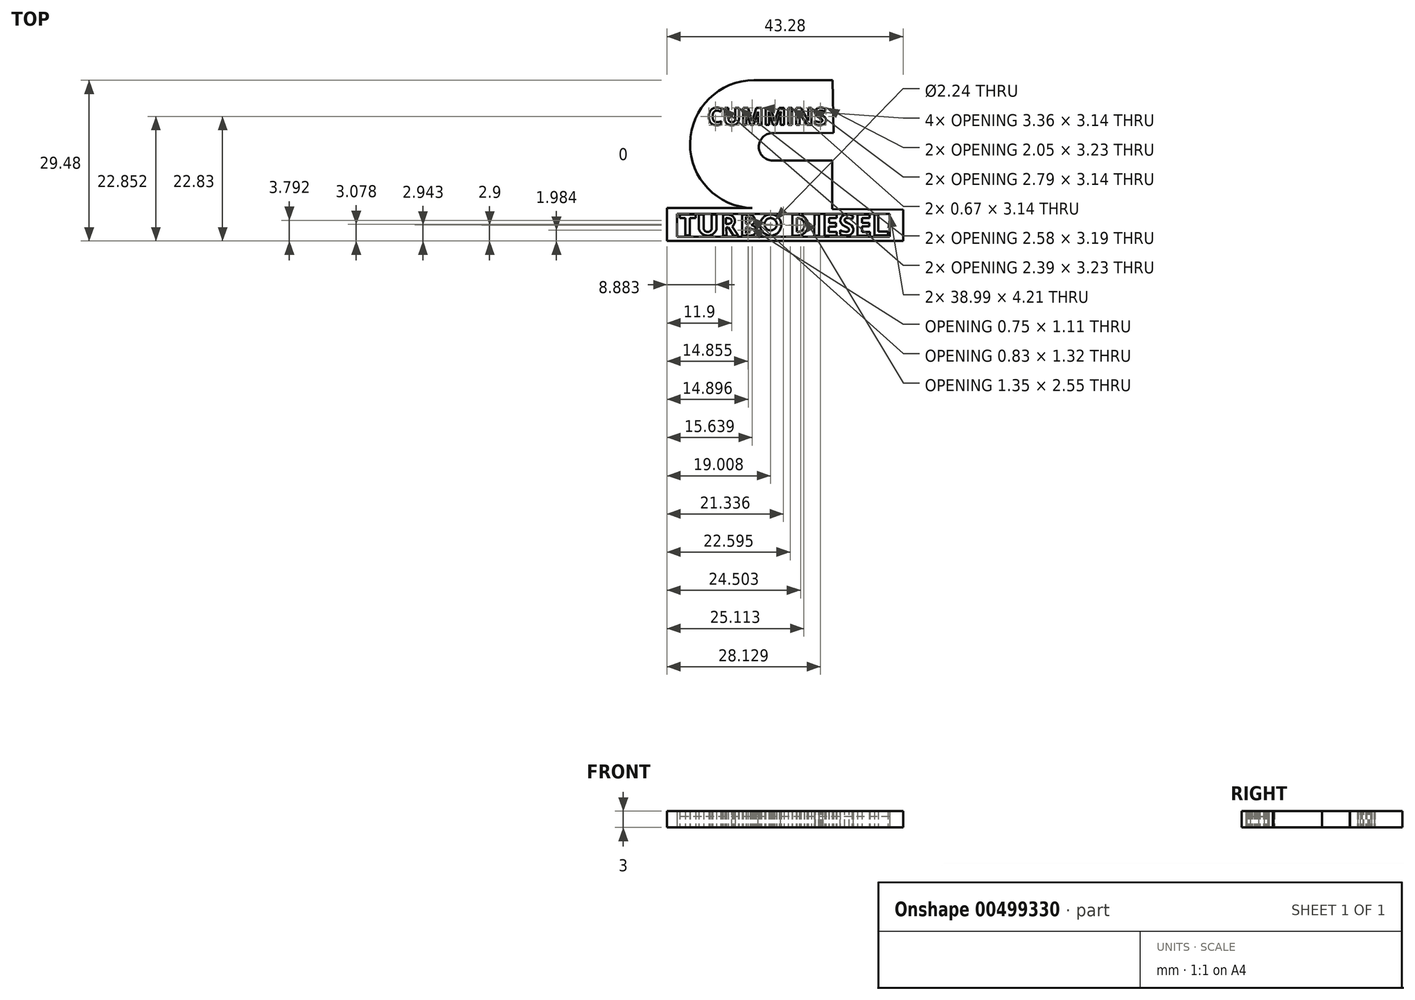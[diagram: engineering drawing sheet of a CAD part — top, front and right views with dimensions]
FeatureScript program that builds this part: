
annotation { "Feature Type Name" : "Feature", "Feature Type Description" : "" }
export const myFeature = defineFeature(function(context is Context, id is Id, definition is map)
    precondition{}
    {
        {
            var Q0;
            Q0=qCreatedBy(makeId("Top.planeOp"),FACE);
            var sketch = newSketch(context, id + "F0", { "sketchPlane" : qUnion([Q0])});
            skLineSegment(sketch, "E0", {"start": v(-58.17, -40.48) * mm, "end": v(-14.89, -40.48) * mm});
            skLineSegment(sketch, "E1", {"start": v(-14.89, -40.48) * mm, "end": v(-14.89, -34.72) * mm});
            skLineSegment(sketch, "E2", {"start": v(-14.89, -34.72) * mm, "end": v(-27.85, -34.6) * mm});
            skLineSegment(sketch, "E3", {"start": v(-27.85, -34.6) * mm, "end": v(-27.85, -25.72) * mm});
            skFitSpline(sketch, "E4", {"points": [v(-27.65, -20.6) * mm, v(-38.88, -20.67) * mm], "startDerivative": vector(-11.23, -0.07) * mm, "endDerivative": vector(-11.23, -0.07) * mm});
            skFitSpline(sketch, "E5", {"points": [v(-27.82, -11) * mm, v(-27.65, -20.6) * mm], "startDerivative": vector(0.17, -9.61) * mm, "endDerivative": vector(0.17, -9.61) * mm});
            skLineSegment(sketch, "E6", {"start": v(-42.53, -34.43) * mm, "end": v(-27.85, -34.6) * mm});
            skLineSegment(sketch, "E7", {"start": v(-27.85, -25.72) * mm, "end": v(-38.8, -25.72) * mm});
            skLineSegment(sketch, "E8", {"start": v(-55.83, -35.61) * mm, "end": v(-55.83, -36.28) * mm});
            skLineSegment(sketch, "E9", {"start": v(-55.83, -36.28) * mm, "end": v(-54.78, -36.28) * mm});
            skLineSegment(sketch, "E10", {"start": v(-54.78, -36.28) * mm, "end": v(-54.78, -39.44) * mm});
            skLineSegment(sketch, "E11", {"start": v(-53.95, -39.44) * mm, "end": v(-53.95, -36.28) * mm});
            skLineSegment(sketch, "E12", {"start": v(-53.95, -36.28) * mm, "end": v(-52.88, -36.28) * mm});
            skLineSegment(sketch, "E13", {"start": v(-52.88, -36.28) * mm, "end": v(-52.88, -35.61) * mm});
            skLineSegment(sketch, "E14", {"start": v(-52.88, -35.61) * mm, "end": v(-55.83, -35.61) * mm});
            skPoint(sketch, "E15", {"position": v(-50.74, -19.2) * mm});
            skText(sketch, "E16", { "text": "CUMMINS", "fontName": "OpenSans-Bold.ttf"});
            skPoint(sketch, "E17", {"position": v(-47.5, -22.36) * mm});
            skLineSegment(sketch, "E18", {"start": v(-47.87, -39.47) * mm, "end": v(-47.22, -39.48) * mm});
            skLineSegment(sketch, "E19", {"start": v(-47.22, -39.48) * mm, "end": v(-47.34, -38) * mm});
            skLineSegment(sketch, "E20", {"start": v(-47.34, -38) * mm, "end": v(-46.9, -38) * mm});
            skLineSegment(sketch, "E21", {"start": v(-46.9, -38) * mm, "end": v(-46, -39.47) * mm});
            skLineSegment(sketch, "E22", {"start": v(-46, -39.47) * mm, "end": v(-45.07, -39.47) * mm});
            skLineSegment(sketch, "E23", {"start": v(-45.07, -39.47) * mm, "end": v(-46.2, -37.8) * mm});
            skLineSegment(sketch, "E24", {"start": v(-52.34, -35.65) * mm, "end": v(-51.45, -35.65) * mm});
            skLineSegment(sketch, "E25", {"start": v(-49.95, -35.6) * mm, "end": v(-49.07, -35.6) * mm});
            skLineSegment(sketch, "E26", {"start": v(-49.95, -35.6) * mm, "end": v(-49.95, -38.21) * mm});
            skPoint(sketch, "E27.7.internal.snap0", {"position": v(-46.45, -38.74) * mm});
            skLineSegment(sketch, "E28", {"start": v(-47.35, -36.28) * mm, "end": v(-47.35, -37.32) * mm});
            skLineSegment(sketch, "E29", {"start": v(-47.35, -36.28) * mm, "end": v(-46.92, -36.28) * mm});
            skFitSpline(sketch, "E30", {"points": [v(-47.35, -37.32) * mm, v(-47.07, -37.32) * mm, v(-46.97, -37.32) * mm, v(-46.66, -37.29) * mm, v(-46.45, -37.16) * mm, v(-46.33, -36.95) * mm, v(-46.32, -36.72) * mm, v(-46.37, -36.55) * mm, v(-46.47, -36.43) * mm, v(-46.6, -36.35) * mm, v(-46.77, -36.3) * mm, v(-46.92, -36.28) * mm], "startDerivative": vector(3.02, 0) * mm, "endDerivative": vector(-1.87, 0.24) * mm});
            skPoint(sketch, "E31.first.point", {"position": v(-38.93, -39.47) * mm});
            skPoint(sketch, "E31.second.point", {"position": v(-38.68, -35.65) * mm});
            skPoint(sketch, "E31.third.point", {"position": v(-41.08, -37.34) * mm});
            skLineSegment(sketch, "E32", {"start": v(-34.34, -36.26) * mm, "end": v(-34.34, -38.8) * mm});
            skLineSegment(sketch, "E33", {"start": v(-31.14, -35.65) * mm, "end": v(-30.31, -35.65) * mm});
            skLineSegment(sketch, "E34", {"start": v(-30.31, -35.65) * mm, "end": v(-30.31, -39.47) * mm});
            skLineSegment(sketch, "E35", {"start": v(-30.31, -39.47) * mm, "end": v(-31.16, -39.47) * mm});
            skLineSegment(sketch, "E36", {"start": v(-31.16, -39.47) * mm, "end": v(-31.14, -35.65) * mm});
            skLineSegment(sketch, "E37", {"start": v(-28.47, -36.27) * mm, "end": v(-27.02, -36.27) * mm});
            skLineSegment(sketch, "E38", {"start": v(-27.02, -36.27) * mm, "end": v(-27.02, -35.65) * mm});
            skLineSegment(sketch, "E39", {"start": v(-27.02, -35.65) * mm, "end": v(-29.3, -35.65) * mm});
            skLineSegment(sketch, "E40", {"start": v(-29.3, -35.65) * mm, "end": v(-29.3, -39.47) * mm});
            skLineSegment(sketch, "E41", {"start": v(-29.3, -39.47) * mm, "end": v(-27.07, -39.47) * mm});
            skLineSegment(sketch, "E42", {"start": v(-27.07, -39.47) * mm, "end": v(-27.07, -38.8) * mm});
            skLineSegment(sketch, "E43", {"start": v(-27.07, -38.8) * mm, "end": v(-28.5, -38.8) * mm});
            skLineSegment(sketch, "E44", {"start": v(-28.5, -38.8) * mm, "end": v(-28.5, -37.84) * mm});
            skLineSegment(sketch, "E45", {"start": v(-28.5, -37.84) * mm, "end": v(-27.18, -37.84) * mm});
            skLineSegment(sketch, "E46", {"start": v(-27.18, -37.84) * mm, "end": v(-27.18, -37.12) * mm});
            skLineSegment(sketch, "E47", {"start": v(-27.18, -37.12) * mm, "end": v(-28.52, -37.12) * mm});
            skLineSegment(sketch, "E48", {"start": v(-28.47, -36.27) * mm, "end": v(-28.47, -37.12) * mm});
            skLineSegment(sketch, "E49", {"start": v(-23.26, -39.48) * mm, "end": v(-20.98, -39.48) * mm});
            skLineSegment(sketch, "E50", {"start": v(-20.98, -38.77) * mm, "end": v(-22.42, -38.77) * mm});
            skLineSegment(sketch, "E51", {"start": v(-22.42, -38.77) * mm, "end": v(-22.42, -37.81) * mm});
            skLineSegment(sketch, "E52", {"start": v(-22.42, -37.81) * mm, "end": v(-21.1, -37.81) * mm});
            skLineSegment(sketch, "E53", {"start": v(-21.1, -37.81) * mm, "end": v(-21.1, -37.13) * mm});
            skLineSegment(sketch, "E54", {"start": v(-21.1, -37.13) * mm, "end": v(-22.44, -37.13) * mm});
            skLineSegment(sketch, "E55", {"start": v(-22.44, -37.13) * mm, "end": v(-22.44, -36.27) * mm});
            skLineSegment(sketch, "E56", {"start": v(-22.44, -36.27) * mm, "end": v(-21, -36.27) * mm});
            skLineSegment(sketch, "E57", {"start": v(-21, -36.27) * mm, "end": v(-21, -35.61) * mm});
            skLineSegment(sketch, "E58", {"start": v(-23.24, -35.61) * mm, "end": v(-23.24, -36.44) * mm});
            skLineSegment(sketch, "E59", {"start": v(-23.24, -36.44) * mm, "end": v(-23.26, -39.48) * mm});
            skLineSegment(sketch, "E60", {"start": v(-20.14, -35.65) * mm, "end": v(-19.4, -35.65) * mm});
            skLineSegment(sketch, "E61", {"start": v(-42.53, -34.43) * mm, "end": v(-58.17, -34.43) * mm});
            skLineSegment(sketch, "E62", {"start": v(-58.17, -34.43) * mm, "end": v(-58.17, -40.48) * mm});
            skLineSegment(sketch, "E63", {"start": v(-54.78, -39.44) * mm, "end": v(-54.78, -39.47) * mm});
            skLineSegment(sketch, "E64", {"start": v(-54.78, -39.47) * mm, "end": v(-53.95, -39.47) * mm});
            skLineSegment(sketch, "E65", {"start": v(-53.95, -39.44) * mm, "end": v(-53.95, -39.47) * mm});
            skLineSegment(sketch, "E66", {"start": v(-52.34, -35.65) * mm, "end": v(-52.34, -38.14) * mm});
            skLineSegment(sketch, "E67", {"start": v(-51.45, -35.65) * mm, "end": v(-51.45, -38.14) * mm});
            skLineSegment(sketch, "E68", {"start": v(-49.07, -35.6) * mm, "end": v(-49.07, -38.21) * mm});
            skArc(sketch, "E69", {"start": v(-51.45, -38.14) * mm, "mid": v(-50.73, -38.81) * mm, "end": v(-49.95, -38.21) * mm});
            skArc(sketch, "E70", {"start": v(-52.34, -38.14) * mm, "mid": v(-50.73, -39.5) * mm, "end": v(-49.07, -38.21) * mm});
            skLineSegment(sketch, "E71", {"start": v(-44.38, -35.65) * mm, "end": v(-44.38, -39.47) * mm});
            skLineSegment(sketch, "E72", {"start": v(-44.38, -35.65) * mm, "end": v(-43.04, -35.65) * mm});
            skArc(sketch, "E73", {"start": v(-42.74, -37.56) * mm, "mid": v(-42.07, -36.48) * mm, "end": v(-43.04, -35.65) * mm});
            skPoint(sketch, "E73.startSnap0", {"position": v(-44.38, -37.56) * mm});
            skLineSegment(sketch, "E74", {"start": v(-44.38, -39.47) * mm, "end": v(-42.76, -39.46) * mm});
            skArc(sketch, "E75", {"start": v(-42.76, -39.46) * mm, "mid": v(-41.8, -38.52) * mm, "end": v(-42.74, -37.56) * mm});
            skCircle(sketch, "E76", {"center": v(-39.16, -37.4) * mm, "radius": 1.12 * mm});
            skLineSegment(sketch, "E77", {"start": v(-35.15, -35.65) * mm, "end": v(-35.15, -39.47) * mm});
            skLineSegment(sketch, "E78", {"start": v(-35.15, -35.65) * mm, "end": v(-34.21, -35.65) * mm});
            skLineSegment(sketch, "E79", {"start": v(-35.15, -39.47) * mm, "end": v(-34.21, -39.47) * mm});
            skArc(sketch, "E80", {"start": v(-32.99, -37.53) * mm, "mid": v(-33.38, -36.59) * mm, "end": v(-34.34, -36.26) * mm});
            skArc(sketch, "E81", {"start": v(-34.34, -38.8) * mm, "mid": v(-33.36, -38.5) * mm, "end": v(-32.99, -37.53) * mm});
            skLineSegment(sketch, "E82", {"start": v(-27.82, -11) * mm, "end": v(-42.2, -11) * mm});
            skArc(sketch, "E83", {"start": v(-42.2, -11) * mm, "mid": v(-53.93, -22.55) * mm, "end": v(-42.53, -34.43) * mm});
            skArc(sketch, "E84", {"start": v(-38.88, -20.67) * mm, "mid": v(-41.32, -23.24) * mm, "end": v(-38.8, -25.72) * mm});
            skLineSegment(sketch, "E85", {"start": v(-47.87, -39.47) * mm, "end": v(-47.87, -35.65) * mm});
            skLineSegment(sketch, "E86", {"start": v(-46.9, -35.65) * mm, "end": v(-47.87, -35.65) * mm});
            skArc(sketch, "E87", {"start": v(-46.2, -37.8) * mm, "mid": v(-45.77, -36.47) * mm, "end": v(-46.9, -35.65) * mm});
            skArc(sketch, "E88", {"start": v(-38.93, -39.47) * mm, "mid": v(-37.22, -37.66) * mm, "end": v(-38.68, -35.65) * mm});
            skArc(sketch, "E89", {"start": v(-38.68, -35.65) * mm, "mid": v(-41.08, -37.41) * mm, "end": v(-38.93, -39.47) * mm});
            skArc(sketch, "E90", {"start": v(-34.21, -39.47) * mm, "mid": v(-32.3, -37.56) * mm, "end": v(-34.21, -35.65) * mm});
            skArc(sketch, "E91", {"start": v(-52.34, -38.14) * mm, "mid": v(-50.73, -39.49) * mm, "end": v(-49.07, -38.21) * mm});
            skLineSegment(sketch, "E92", {"start": v(-47.87, -35.65) * mm, "end": v(-47.87, -39.47) * mm});
            skLineSegment(sketch, "E93", {"start": v(-47.87, -35.65) * mm, "end": v(-46.9, -35.65) * mm});
            skLineSegment(sketch, "E94", {"start": v(-46.2, -37.8) * mm, "end": v(-45.07, -39.47) * mm});
            skLineSegment(sketch, "E95", {"start": v(-46, -39.47) * mm, "end": v(-46.9, -38) * mm});
            skLineSegment(sketch, "E96", {"start": v(-47.34, -38) * mm, "end": v(-47.22, -39.48) * mm});
            skCircle(sketch, "E97", {"center": v(-39.16, -37.4) * mm, "radius": 1.11 * mm});
            skLineSegment(sketch, "E98", {"start": v(-43.7, -36.03) * mm, "end": v(-43.7, -37.35) * mm});
            skArc(sketch, "E99", {"start": v(-43.7, -37.35) * mm, "mid": v(-42.86, -36.69) * mm, "end": v(-43.7, -36.03) * mm});
            skLineSegment(sketch, "E100", {"start": v(-43.7, -37.97) * mm, "end": v(-43.68, -39.02) * mm});
            skArc(sketch, "E101", {"start": v(-43.68, -39.02) * mm, "mid": v(-42.94, -38.5) * mm, "end": v(-43.7, -37.97) * mm});
            skLineSegment(sketch, "E102", {"start": v(-24.01, -35.87) * mm, "end": v(-24.27, -36.49) * mm});
            skFitSpline(sketch, "E103", {"points": [v(-24.27, -36.49) * mm, v(-24.4, -36.44) * mm, v(-24.56, -36.38) * mm, v(-24.76, -36.32) * mm, v(-24.94, -36.29) * mm, v(-25.02, -36.28) * mm, v(-25.23, -36.27) * mm, v(-25.37, -36.3) * mm, v(-25.5, -36.36) * mm, v(-25.6, -36.54) * mm, v(-25.6, -36.74) * mm, v(-25.54, -36.87) * mm, v(-25.4, -37) * mm, v(-24.71, -37.35) * mm, v(-24.27, -37.65) * mm, v(-24.04, -38.02) * mm, v(-23.99, -38.37) * mm, v(-24.06, -38.8) * mm, v(-24.27, -39.1) * mm, v(-24.56, -39.3) * mm, v(-24.9, -39.41) * mm, v(-25.14, -39.46) * mm, v(-25.3, -39.46) * mm, v(-25.47, -39.46) * mm, v(-25.78, -39.44) * mm, v(-26.08, -39.38) * mm, v(-26.44, -39.24) * mm], "startDerivative": vector(-4.34, 1.57) * mm, "endDerivative": vector(-7.91, 3.38) * mm});
            skLineSegment(sketch, "E104", {"start": v(-26.44, -38.5) * mm, "end": v(-26.44, -39.24) * mm});
            skFitSpline(sketch, "E105", {"points": [v(-26.44, -38.5) * mm, v(-26, -38.68) * mm, v(-25.71, -38.76) * mm, v(-25.38, -38.8) * mm, v(-25.17, -38.8) * mm, v(-24.99, -38.75) * mm, v(-24.87, -38.67) * mm, v(-24.8, -38.56) * mm, v(-24.77, -38.38) * mm, v(-24.83, -38.22) * mm, v(-24.93, -38.12) * mm, v(-25.1, -38) * mm, v(-25.23, -37.93) * mm, v(-25.83, -37.63) * mm, v(-26.22, -37.27) * mm, v(-26.38, -36.85) * mm, v(-26.38, -36.47) * mm, v(-26.23, -36.1) * mm, v(-26, -35.85) * mm, v(-25.74, -35.7) * mm, v(-25.37, -35.62) * mm, v(-25.21, -35.61) * mm, v(-25.13, -35.61) * mm, v(-25, -35.61) * mm, v(-24.96, -35.61) * mm, v(-24.68, -35.65) * mm, v(-24.42, -35.72) * mm, v(-24.01, -35.87) * mm], "startDerivative": vector(9.09, -3.88) * mm, "endDerivative": vector(9.18, -3.55) * mm});
            skLineSegment(sketch, "E106", {"start": v(-23.24, -35.61) * mm, "end": v(-21, -35.61) * mm});
            skLineSegment(sketch, "E107", {"start": v(-20.14, -35.65) * mm, "end": v(-20.14, -39.42) * mm});
            skLineSegment(sketch, "E108", {"start": v(-20.14, -39.42) * mm, "end": v(-17.67, -39.42) * mm});
            skLineSegment(sketch, "E109", {"start": v(-17.67, -39.42) * mm, "end": v(-17.67, -38.72) * mm});
            skLineSegment(sketch, "E110", {"start": v(-17.67, -38.72) * mm, "end": v(-19.42, -38.72) * mm});
            skLineSegment(sketch, "E111", {"start": v(-19.42, -38.72) * mm, "end": v(-19.4, -35.65) * mm});
            skLineSegment(sketch, "E112", {"start": v(-19.4, -35.65) * mm, "end": v(-20.14, -35.65) * mm});
            skLineSegment(sketch, "E113", {"start": v(-56.33, -35.47) * mm, "end": v(-56.33, -39.69) * mm});
            skLineSegment(sketch, "E114", {"start": v(-56.33, -39.69) * mm, "end": v(-17.34, -39.69) * mm});
            skLineSegment(sketch, "E115", {"start": v(-17.34, -39.69) * mm, "end": v(-17.34, -35.48) * mm});
            skLineSegment(sketch, "E116", {"start": v(-17.34, -35.48) * mm, "end": v(-56.33, -35.47) * mm});
            skLineSegment(sketch, "E117", {"start": v(-20.98, -38.77) * mm, "end": v(-20.98, -39.48) * mm});
            skLineSegment(sketch, "E118", {"start": v(-52.88, -35.61) * mm, "end": v(-52.88, -36.28) * mm});
            skLineSegment(sketch, "E119", {"start": v(-54.78, -39.44) * mm, "end": v(-53.95, -39.44) * mm});
            const initialGuessF0  = {"E16": [-0.05074, -0.0192, 1, 0, 0.00317]};
            skSetInitialGuess(sketch, initialGuessF0);
            skSolve(sketch);
        }
        {
            var Q0;
            {var subQ25=sQuery(id+"F0.wireOp",EDGE,"30c9a4f5-6872-4423-ba19-b8290065d747.sketch_text.stroke-0");Q0=makeQuery(id+"F0.imprint","IMPRINT",FACE,{"disambiguationData":[TD([[makeQuery(id+"F0.imprint","IMPRINT",EDGE,{"derivedFrom":subQ25}),-1.0]])]});}
            var Q1;
            Q1=makeQuery(id+"F0.imprint","IMPRINT",FACE,{"disambiguationData":[TD([[makeQuery(id+"F0.imprint","IMPRINT",EDGE,{"derivedFrom":sQuery(id+"F0.wireOp",EDGE,"E37")}),1.0]])]});
            var Q2;
            Q2=makeQuery(id+"F0.imprint","IMPRINT",FACE,{"disambiguationData":[TD([[makeQuery(id+"F0.imprint","IMPRINT",EDGE,{"derivedFrom":sQuery(id+"F0.wireOp",EDGE,"E33")}),-1.0]])]});
            var Q3;
            Q3=makeQuery(id+"F0.imprint","IMPRINT",FACE,{"disambiguationData":[TD([[makeQuery(id+"F0.imprint","IMPRINT",EDGE,{"derivedFrom":sQuery(id+"F0.wireOp",EDGE,"E32")}),-1.0]])]});
            var Q4;
            Q4=makeQuery(id+"F0.imprint","IMPRINT",FACE,{"disambiguationData":[TD([[makeQuery(id+"F0.imprint","IMPRINT",EDGE,{"derivedFrom":sQuery(id+"F0.wireOp",EDGE,"E76")}),-1.0]])]});
            var Q5;
            Q5=makeQuery(id+"F0.imprint","IMPRINT",FACE,{"disambiguationData":[TD([[makeQuery(id+"F0.imprint","IMPRINT",EDGE,{"derivedFrom":sQuery(id+"F0.wireOp",EDGE,"E3")}),1.0]])]});
            var Q6;
            Q6=makeQuery(id+"F0.imprint","IMPRINT",FACE,{"disambiguationData":[TD([[makeQuery(id+"F0.imprint","IMPRINT",EDGE,{"derivedFrom":sQuery(id+"F0.wireOp",EDGE,"E0")}),1.0]])]});
            var Q7;
            Q7=makeQuery(id+"F0.imprint","IMPRINT",FACE,{"disambiguationData":[TD([[makeQuery(id+"F0.imprint","IMPRINT",EDGE,{"derivedFrom":sQuery(id+"F0.wireOp",EDGE,"E107")}),1.0]])]});
            var Q8;
            Q8=makeQuery(id+"F0.imprint","IMPRINT",FACE,{"disambiguationData":[TD([[makeQuery(id+"F0.imprint","IMPRINT",EDGE,{"derivedFrom":sQuery(id+"F0.wireOp",EDGE,"E71")}),1.0]])]});
            var Q9;
            Q9=makeQuery(id+"F0.imprint","IMPRINT",FACE,{"disambiguationData":[TD([[makeQuery(id+"F0.imprint","IMPRINT",EDGE,{"derivedFrom":sQuery(id+"F0.wireOp",EDGE,"E28")}),-1.0]])]});
            var Q10;
            Q10=makeQuery(id+"F0.imprint","IMPRINT",FACE,{"disambiguationData":[TD([[makeQuery(id+"F0.imprint","IMPRINT",EDGE,{"derivedFrom":sQuery(id+"F0.wireOp",EDGE,"E25")}),-1.0]])]});
            extrude(context, id + "F1", {"entities" : qUnion([Q0, Q1, Q2, Q3, Q4, Q5, Q6, Q7, Q8, Q9, Q10]), "depth" : 3 * mm, "offsetDistance" : 25 * mm});
        }
        {
            var Q0;
            Q0 = qSketchRegion(id + "F0", true);
            var Q1;
            Q1=makeQuery(id+"F0.imprint","IMPRINT",FACE,{"disambiguationData":[TD([[makeQuery(id+"F0.imprint","IMPRINT",EDGE,{"derivedFrom":sQuery(id+"F0.wireOp",EDGE,"E9")}),1.0]])]});
            var Q2;
            Q2=makeQuery(id+"F0.imprint","IMPRINT",FACE,{"disambiguationData":[TD([[makeQuery(id+"F0.imprint","IMPRINT",EDGE,{"derivedFrom":sQuery(id+"F0.wireOp",EDGE,"E49")}),1.0]])]});
            var Q3;
            Q3=makeQuery(id+"F0.imprint","IMPRINT",FACE,{"disambiguationData":[TD([[makeQuery(id+"F0.imprint","IMPRINT",EDGE,{"derivedFrom":sQuery(id+"F0.wireOp",EDGE,"E102")}),-1.0]])]});
            extrude(context, id + "F2", {"entities" : qUnion([Q0, Q1, Q2, Q3]), "depth" : 3 * mm, "offsetDistance" : 25 * mm});
        }
        {
            var Q0;
            Q0=makeQuery(id+"F0.imprint","IMPRINT",FACE,{"disambiguationData":[TD([[makeQuery(id+"F0.imprint","IMPRINT",EDGE,{"derivedFrom":sQuery(id+"F0.wireOp",EDGE,"E0")}),1.0]])]});
            var sketch = newSketch(context, id + "F3", { "sketchPlane" : qUnion([Q0])});
            skLineSegment(sketch, "E120.0.0", {"start": v(-27.85, -34.6) * mm, "end": v(-42.53, -34.43) * mm});
            skLineSegment(sketch, "E120.0.1", {"start": v(-42.53, -34.43) * mm, "end": v(-58.17, -34.43) * mm});
            skLineSegment(sketch, "E120.0.2", {"start": v(-58.17, -34.43) * mm, "end": v(-58.17, -40.48) * mm});
            skLineSegment(sketch, "E120.0.3", {"start": v(-58.17, -40.48) * mm, "end": v(-14.89, -40.48) * mm});
            skLineSegment(sketch, "E120.0.4", {"start": v(-14.89, -40.48) * mm, "end": v(-14.89, -34.72) * mm});
            skLineSegment(sketch, "E120.0.5", {"start": v(-14.89, -34.72) * mm, "end": v(-27.85, -34.6) * mm});
            skSolve(sketch);
        }
        {
            var Q0;
            Q0=makeQuery(id+"F3.imprint","IMPRINT",FACE,{"disambiguationData":[TD([[makeQuery(id+"F3.imprint","IMPRINT",EDGE,{"derivedFrom":makeQuery(id+"F0.imprint","IMPRINT",EDGE,{"derivedFrom":sQuery(id+"F0.wireOp",EDGE,"E113")})}),1.0]])]});
            extrude(context, id + "F4", {"entities" : qUnion([Q0]), "depth" : 2 * mm, "offsetDistance" : 25 * mm});
        }
    });
